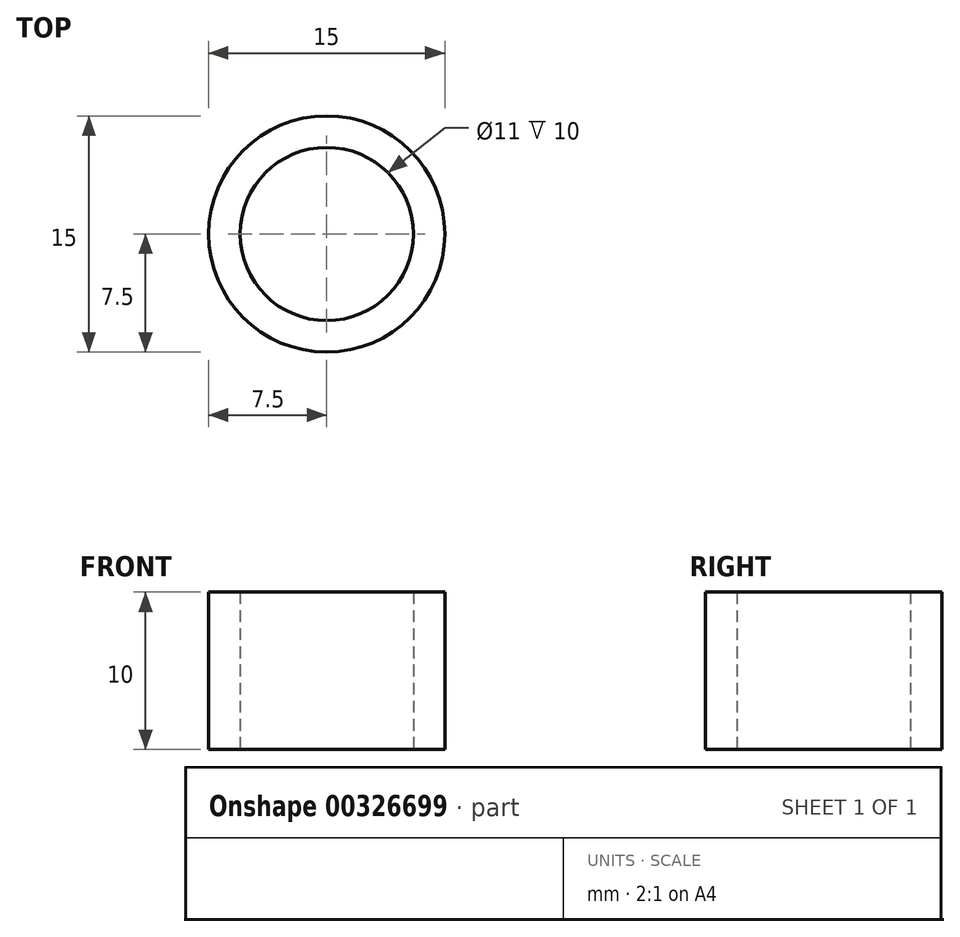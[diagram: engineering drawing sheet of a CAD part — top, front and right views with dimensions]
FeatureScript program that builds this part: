
annotation { "Feature Type Name" : "Feature", "Feature Type Description" : "" }
export const myFeature = defineFeature(function(context is Context, id is Id, definition is map)
    precondition{}
    {
        {
            var Q0;
            Q0=qCreatedBy(makeId("Top.planeOp"),FACE);
            var sketch = newSketch(context, id + "F0", { "sketchPlane" : qUnion([Q0])});
            skCircle(sketch, "E0.2.0.0", {"center": v(40, 0) * mm, "radius": 5.5 * mm});
            skCircle(sketch, "E0.2.0.1", {"center": v(40, 0) * mm, "radius": 7.5 * mm});
            skSolve(sketch);
        }
        {
            var Q0;
            Q0=makeQuery(id+"F0.imprint","IMPRINT",FACE,{"disambiguationData":[TD([[makeQuery(id+"F0.imprint","IMPRINT",EDGE,{"derivedFrom":sQuery(id+"F0.wireOp",EDGE,"E0.2.0.0")}),-1.0]])]});
            extrude(context, id + "F1", {"entities" : qUnion([Q0]), "depth" : 10 * mm});
        }
    });
